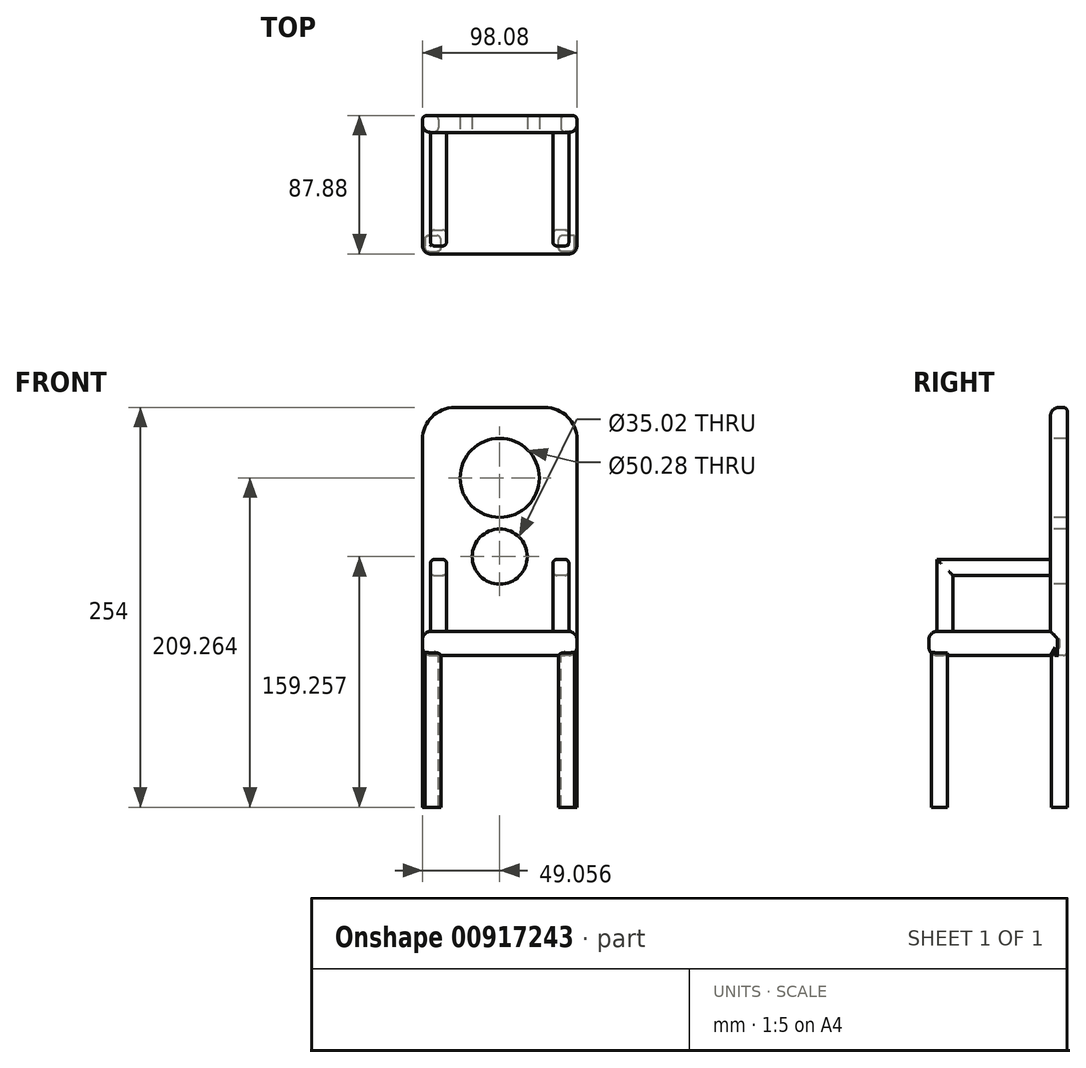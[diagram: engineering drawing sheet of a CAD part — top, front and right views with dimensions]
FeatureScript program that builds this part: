
annotation { "Feature Type Name" : "Feature", "Feature Type Description" : "" }
export const myFeature = defineFeature(function(context is Context, id is Id, definition is map)
    precondition{}
    {
        {
            var Q0;
            Q0=qCreatedBy(makeId("Top.planeOp"),FACE);
            var sketch = newSketch(context, id + "F0", { "sketchPlane" : qUnion([Q0])});
            skLineSegment(sketch, "E0.bottom", {"start": v(-206.15, 232.77) * mm, "end": v(284.07, 232.77) * mm});
            skLineSegment(sketch, "E0.top", {"start": v(-206.15, -181.25) * mm, "end": v(284.07, -181.25) * mm});
            skLineSegment(sketch, "E0.left", {"start": v(-206.15, 232.77) * mm, "end": v(-206.15, -181.25) * mm});
            skLineSegment(sketch, "E0.right", {"start": v(284.07, 232.77) * mm, "end": v(284.07, -181.25) * mm});
            skSolve(sketch);
        }
        {
            var Q0;
            Q0=qSketchRegion(id+"F0",true);
            extrude(context, id + "F1", {"entities" : qUnion([Q0]), "depth" : 76.2 * mm, "offsetDistance" : 25.4 * mm});
        }
        {
            var Q0;
            Q0=makeQuery(id+"F1.opExtrude","CAP_EDGE",EDGE,{"disambiguationData":[OSD([sQuery(id+"F0.wireOp",EDGE,"E0.top")])],"isStart":false});
            var Q1;
            Q1=makeQuery(id+"F1.opExtrude","CAP_EDGE",EDGE,{"disambiguationData":[OSD([sQuery(id+"F0.wireOp",EDGE,"E0.left")])],"isStart":false});
            var Q2;
            Q2=makeQuery(id+"F1.opExtrude","SWEPT_EDGE",EDGE,{"disambiguationData":[OSD([sQuery(id+"F0.wireOp",EDGE,"E0.top"),sQuery(id+"F0.wireOp",EDGE,"E0.left")])]});
            var Q3;
            Q3=makeQuery(id+"F1.opExtrude","SWEPT_EDGE",EDGE,{"disambiguationData":[OSD([sQuery(id+"F0.wireOp",EDGE,"E0.top"),sQuery(id+"F0.wireOp",EDGE,"E0.right")])]});
            var Q4;
            Q4=makeQuery(id+"F1.opExtrude","CAP_EDGE",EDGE,{"disambiguationData":[OSD([sQuery(id+"F0.wireOp",EDGE,"E0.right")])],"isStart":false});
            fillet(context, id + "F2", {"entities" : qUnion([Q0, Q1, Q2, Q3, Q4]), "radius" : 25.4 * mm, "tangentPropagation" : true, "allowEdgeOverflow" : false});
        }
        {
            var Q0;
            Q0=makeQuery(id+"F1.opExtrude","SWEPT_FACE",FACE,{"disambiguationData":[OSD([sQuery(id+"F0.wireOp",EDGE,"E0.bottom")])]});
            cPlane(context, id + "F3", {"entities" : qUnion([Q0]), "cplaneType" : CPlaneType.OFFSET, "offset" : 25.4 * mm, "width" : 152.4 * mm, "height" : 152.4 * mm});
        }
        {
            var Q0;
            Q0=qCreatedBy(id+"F3.planeOp",FACE);
            var sketch = newSketch(context, id + "F4", { "sketchPlane" : qUnion([Q0])});
            skLineSegment(sketch, "E1.bottom", {"start": v(-284.24, 0) * mm, "end": v(205.98, 0) * mm});
            skLineSegment(sketch, "E1.top", {"start": v(-284.24, 787.4) * mm, "end": v(205.98, 787.4) * mm});
            skLineSegment(sketch, "E1.left", {"start": v(-284.24, 0) * mm, "end": v(-284.24, 787.4) * mm});
            skLineSegment(sketch, "E1.right", {"start": v(205.98, 0) * mm, "end": v(205.98, 787.4) * mm});
            skSolve(sketch);
        }
        {
            var Q0;
            Q0=qSketchRegion(id+"F4",true);
            extrude(context, id + "F5", {"entities" : qUnion([Q0]), "operationType" : NewBodyOperationType.ADD, "oppositeDirection" : true, "depth" : 53.34 * mm, "offsetDistance" : 25.4 * mm});
        }
        {
            var Q0;
            Q0=makeQuery(id+"F5.opExtrude","SWEPT_EDGE",EDGE,{"disambiguationData":[OSD([sQuery(id+"F4.wireOp",EDGE,"E1.top"),sQuery(id+"F4.wireOp",EDGE,"E1.left")])]});
            var Q1;
            Q1=makeQuery(id+"F5.opExtrude","SWEPT_EDGE",EDGE,{"disambiguationData":[OSD([sQuery(id+"F4.wireOp",EDGE,"E1.top"),sQuery(id+"F4.wireOp",EDGE,"E1.right")])]});
            fillet(context, id + "F6", {"entities" : qUnion([Q0, Q1]), "radius" : 101.6 * mm, "tangentPropagation" : true, "allowEdgeOverflow" : false});
        }
        {
            var Q0;
            Q0=makeQuery(id+"F5.opExtrude","CAP_EDGE",EDGE,{"disambiguationData":[OSD([sQuery(id+"F4.wireOp",EDGE,"E1.left")])],"isStart":false});
            fillet(context, id + "F7", {"entities" : qUnion([Q0]), "radius" : 25.4 * mm, "tangentPropagation" : true, "allowEdgeOverflow" : false});
        }
        {
            var Q0;
            Q0=makeQuery(id+"F5.boolean.opBoolean","MERGE",FACE,{"derivedFrom":[makeQuery(id+"F1.opExtrude","CAP_FACE",FACE,{"disambiguationData":[OSD([sQuery(id+"F0.wireOp",EDGE,"E0.bottom"),sQuery(id+"F0.wireOp",EDGE,"E0.top"),sQuery(id+"F0.wireOp",EDGE,"E0.left"),sQuery(id+"F0.wireOp",EDGE,"E0.right")])],"isStart":true}),makeQuery(id+"F5.opExtrude","SWEPT_FACE",FACE,{"disambiguationData":[OSD([sQuery(id+"F4.wireOp",EDGE,"E1.bottom")])]})]});
            var sketch = newSketch(context, id + "F8", { "sketchPlane" : qUnion([Q0])});
            skLineSegment(sketch, "E2.bottom", {"start": v(-198.7, 173.81) * mm, "end": v(-147.9, 173.81) * mm});
            skLineSegment(sketch, "E2.top", {"start": v(-198.7, 123.01) * mm, "end": v(-147.9, 123.01) * mm});
            skLineSegment(sketch, "E2.left", {"start": v(-198.7, 173.81) * mm, "end": v(-198.7, 123.01) * mm});
            skLineSegment(sketch, "E2.right", {"start": v(-147.9, 173.81) * mm, "end": v(-147.9, 123.01) * mm});
            skLineSegment(sketch, "E3.bottom", {"start": v(276.63, 173.81) * mm, "end": v(225.83, 173.81) * mm});
            skLineSegment(sketch, "E3.top", {"start": v(276.63, 123.01) * mm, "end": v(225.83, 123.01) * mm});
            skLineSegment(sketch, "E3.left", {"start": v(276.63, 173.81) * mm, "end": v(276.63, 123.01) * mm});
            skLineSegment(sketch, "E3.right", {"start": v(225.83, 173.81) * mm, "end": v(225.83, 123.01) * mm});
            skLineSegment(sketch, "E4.bottom", {"start": v(284.24, -258.17) * mm, "end": v(233.44, -258.17) * mm});
            skLineSegment(sketch, "E4.top", {"start": v(284.24, -207.37) * mm, "end": v(233.44, -207.37) * mm});
            skLineSegment(sketch, "E4.left", {"start": v(284.24, -258.17) * mm, "end": v(284.24, -207.37) * mm});
            skLineSegment(sketch, "E4.right", {"start": v(233.44, -258.17) * mm, "end": v(233.44, -207.37) * mm});
            skLineSegment(sketch, "E5.bottom", {"start": v(-205.98, -258.17) * mm, "end": v(-155.18, -258.17) * mm});
            skLineSegment(sketch, "E5.top", {"start": v(-205.98, -207.37) * mm, "end": v(-155.18, -207.37) * mm});
            skLineSegment(sketch, "E5.left", {"start": v(-205.98, -258.17) * mm, "end": v(-205.98, -207.37) * mm});
            skLineSegment(sketch, "E5.right", {"start": v(-155.18, -258.17) * mm, "end": v(-155.18, -207.37) * mm});
            skSolve(sketch);
        }
        {
            var Q0;
            Q0=qSketchRegion(id+"F8",true);
            extrude(context, id + "F9", {"entities" : qUnion([Q0]), "operationType" : NewBodyOperationType.ADD, "depth" : 482.6 * mm, "offsetDistance" : 25.4 * mm});
        }
        {
            var Q0;
            Q0=makeQuery(id+"F5.opExtrude","CAP_FACE",FACE,{"disambiguationData":[OSD([sQuery(id+"F4.wireOp",EDGE,"E1.bottom"),sQuery(id+"F4.wireOp",EDGE,"E1.top"),sQuery(id+"F4.wireOp",EDGE,"E1.left"),sQuery(id+"F4.wireOp",EDGE,"E1.right")])],"isStart":false});
            var sketch = newSketch(context, id + "F10", { "sketchPlane" : qUnion([Q0])});
            skCircle(sketch, "E6", {"center": v(39.13, 563.72) * mm, "radius": 125.7 * mm});
            skPoint(sketch, "E6.centerSnap0", {"position": v(39.13, 762) * mm});
            skCircle(sketch, "E7", {"center": v(39.13, 313.69) * mm, "radius": 87.54 * mm});
            skSolve(sketch);
        }
        {
            var Q0;
            Q0=qSketchRegion(id+"F10",true);
            extrude(context, id + "F11", {"entities" : qUnion([Q0]), "operationType" : NewBodyOperationType.REMOVE, "oppositeDirection" : true, "depth" : 320.04 * mm, "offsetDistance" : 25.4 * mm});
        }
        {
            var Q0;
            Q0=makeQuery(id+"F9.opExtrude","SWEPT_EDGE",EDGE,{"disambiguationData":[OSD([sQuery(id+"F0.wireOp",EDGE,"E0.bottom"),sQuery(id+"F0.wireOp",EDGE,"E0.top"),sQuery(id+"F0.wireOp",EDGE,"E0.left"),sQuery(id+"F0.wireOp",EDGE,"E0.right"),sQuery(id+"F8.wireOp",EDGE,"E2.bottom"),sQuery(id+"F8.wireOp",EDGE,"E2.left")])]});
            var Q1;
            Q1=makeQuery(id+"F9.opExtrude","SWEPT_EDGE",EDGE,{"disambiguationData":[OSD([sQuery(id+"F8.wireOp",EDGE,"E2.bottom"),sQuery(id+"F8.wireOp",EDGE,"E2.right")])]});
            var Q2;
            Q2=makeQuery(id+"F9.opExtrude","SWEPT_EDGE",EDGE,{"disambiguationData":[OSD([sQuery(id+"F8.wireOp",EDGE,"E2.top"),sQuery(id+"F8.wireOp",EDGE,"E2.right")])]});
            var Q3;
            Q3=makeQuery(id+"F9.opExtrude","SWEPT_EDGE",EDGE,{"disambiguationData":[OSD([sQuery(id+"F8.wireOp",EDGE,"E2.top"),sQuery(id+"F8.wireOp",EDGE,"E2.left")])]});
            var Q4;
            Q4=makeQuery(id+"F9.opExtrude","SWEPT_EDGE",EDGE,{"disambiguationData":[OSD([sQuery(id+"F8.wireOp",EDGE,"E5.top"),sQuery(id+"F8.wireOp",EDGE,"E5.left")])]});
            var Q5;
            Q5=makeQuery(id+"F9.opExtrude","SWEPT_EDGE",EDGE,{"disambiguationData":[OSD([sQuery(id+"F8.wireOp",EDGE,"E5.top"),sQuery(id+"F8.wireOp",EDGE,"E5.right")])]});
            var Q6;
            Q6=makeQuery(id+"F9.boolean.opBoolean","MERGE",EDGE,{"derivedFrom":[makeQuery(id+"F5.opExtrude","CAP_EDGE",EDGE,{"disambiguationData":[OSD([sQuery(id+"F4.wireOp",EDGE,"E1.right")])],"isStart":true}),makeQuery(id+"F9.opExtrude","SWEPT_EDGE",EDGE,{"disambiguationData":[OSD([sQuery(id+"F8.wireOp",EDGE,"E5.bottom"),sQuery(id+"F8.wireOp",EDGE,"E5.left")])]})]});
            var Q7;
            Q7=makeQuery(id+"F9.opExtrude","SWEPT_EDGE",EDGE,{"disambiguationData":[OSD([sQuery(id+"F4.wireOp",EDGE,"E1.bottom"),sQuery(id+"F8.wireOp",EDGE,"E5.bottom"),sQuery(id+"F8.wireOp",EDGE,"E5.right")])]});
            var Q8;
            Q8=makeQuery(id+"F5.opExtrude","CAP_EDGE",EDGE,{"disambiguationData":[OSD([sQuery(id+"F4.wireOp",EDGE,"E1.bottom")])],"isStart":true});
            var Q9;
            Q9=makeQuery(id+"F9.opExtrude","SWEPT_EDGE",EDGE,{"disambiguationData":[OSD([sQuery(id+"F4.wireOp",EDGE,"E1.bottom"),sQuery(id+"F8.wireOp",EDGE,"E4.bottom"),sQuery(id+"F8.wireOp",EDGE,"E4.right")])]});
            var Q10;
            Q10=makeQuery(id+"F9.boolean.opBoolean","MERGE",EDGE,{"derivedFrom":[makeQuery(id+"F5.opExtrude","CAP_EDGE",EDGE,{"disambiguationData":[OSD([sQuery(id+"F4.wireOp",EDGE,"E1.left")])],"isStart":true}),makeQuery(id+"F9.opExtrude","SWEPT_EDGE",EDGE,{"disambiguationData":[OSD([sQuery(id+"F8.wireOp",EDGE,"E4.bottom"),sQuery(id+"F8.wireOp",EDGE,"E4.left")])]})]});
            var Q11;
            Q11=makeQuery(id+"F9.opExtrude","SWEPT_EDGE",EDGE,{"disambiguationData":[OSD([sQuery(id+"F8.wireOp",EDGE,"E4.top"),sQuery(id+"F8.wireOp",EDGE,"E4.left")])]});
            var Q12;
            Q12=makeQuery(id+"F9.opExtrude","SWEPT_EDGE",EDGE,{"disambiguationData":[OSD([sQuery(id+"F8.wireOp",EDGE,"E4.top"),sQuery(id+"F8.wireOp",EDGE,"E4.right")])]});
            var Q13;
            Q13=makeQuery(id+"F9.opExtrude","SWEPT_EDGE",EDGE,{"disambiguationData":[OSD([sQuery(id+"F8.wireOp",EDGE,"E3.bottom"),sQuery(id+"F8.wireOp",EDGE,"E3.right")])]});
            var Q14;
            Q14=makeQuery(id+"F9.opExtrude","SWEPT_EDGE",EDGE,{"disambiguationData":[OSD([sQuery(id+"F8.wireOp",EDGE,"E3.top"),sQuery(id+"F8.wireOp",EDGE,"E3.right")])]});
            var Q15;
            Q15=makeQuery(id+"F9.opExtrude","SWEPT_EDGE",EDGE,{"disambiguationData":[OSD([sQuery(id+"F0.wireOp",EDGE,"E0.bottom"),sQuery(id+"F0.wireOp",EDGE,"E0.top"),sQuery(id+"F0.wireOp",EDGE,"E0.left"),sQuery(id+"F0.wireOp",EDGE,"E0.right"),sQuery(id+"F8.wireOp",EDGE,"E3.bottom"),sQuery(id+"F8.wireOp",EDGE,"E3.left")])]});
            fillet(context, id + "F12", {"entities" : qUnion([Q0, Q1, Q2, Q3, Q4, Q5, Q6, Q7, Q8, Q9, Q10, Q11, Q12, Q13, Q14, Q15]), "radius" : 12.7 * mm, "tangentPropagation" : true, "allowEdgeOverflow" : false});
        }
        {
            var Q0;
            Q0=makeQuery(id+"F1.opExtrude","CAP_EDGE",EDGE,{"disambiguationData":[OSD([sQuery(id+"F0.wireOp",EDGE,"E0.top")])],"isStart":true});
            fillet(context, id + "F13", {"entities" : qUnion([Q0]), "radius" : 25.4 * mm, "tangentPropagation" : true, "allowEdgeOverflow" : false});
        }
        {
            var Q0;
            Q0=makeQuery(id+"F11.boolean.opBoolean","COPY",EDGE,{"derivedFrom":makeQuery(id+"F11.opExtrude","CAP_EDGE",EDGE,{"disambiguationData":[OSD([sQuery(id+"F10.wireOp",EDGE,"E6")])],"isStart":true})});
            var Q1;
            Q1=makeQuery(id+"F11.boolean.opBoolean","INTERSECT",EDGE,{"derivedFrom":[makeQuery(id+"F9.boolean.opBoolean","MERGE",FACE,{"derivedFrom":[makeQuery(id+"F5.opExtrude","CAP_FACE",FACE,{"disambiguationData":[OSD([sQuery(id+"F4.wireOp",EDGE,"E1.bottom"),sQuery(id+"F4.wireOp",EDGE,"E1.top"),sQuery(id+"F4.wireOp",EDGE,"E1.left"),sQuery(id+"F4.wireOp",EDGE,"E1.right")])],"isStart":true}),makeQuery(id+"F9.opExtrude","SWEPT_FACE",FACE,{"disambiguationData":[OSD([sQuery(id+"F8.wireOp",EDGE,"E4.bottom")])]}),makeQuery(id+"F9.opExtrude","SWEPT_FACE",FACE,{"disambiguationData":[OSD([sQuery(id+"F8.wireOp",EDGE,"E5.bottom")])]})]}),makeQuery(id+"F11.opExtrude","SWEPT_FACE",FACE,{"disambiguationData":[OSD([sQuery(id+"F10.wireOp",EDGE,"E6")])]})]});
            fillet(context, id + "F14", {"entities" : qUnion([Q0, Q1]), "radius" : 5.08 * mm, "tangentPropagation" : true, "allowEdgeOverflow" : false});
        }
        {
            var Q0;
            Q0=makeQuery(id+"F1.opExtrude","CAP_FACE",FACE,{"disambiguationData":[OSD([sQuery(id+"F0.wireOp",EDGE,"E0.bottom"),sQuery(id+"F0.wireOp",EDGE,"E0.top"),sQuery(id+"F0.wireOp",EDGE,"E0.left"),sQuery(id+"F0.wireOp",EDGE,"E0.right")])],"isStart":false});
            var sketch = newSketch(context, id + "F15", { "sketchPlane" : qUnion([Q0])});
            skLineSegment(sketch, "E8.bottom", {"start": v(258.67, -155.85) * mm, "end": v(207.87, -155.85) * mm});
            skLineSegment(sketch, "E8.top", {"start": v(258.67, -105.05) * mm, "end": v(207.87, -105.05) * mm});
            skLineSegment(sketch, "E8.left", {"start": v(258.67, -155.85) * mm, "end": v(258.67, -105.05) * mm});
            skLineSegment(sketch, "E8.right", {"start": v(207.87, -155.85) * mm, "end": v(207.87, -105.05) * mm});
            skLineSegment(sketch, "E9.bottom", {"start": v(-180.75, -155.85) * mm, "end": v(-129.95, -155.85) * mm});
            skLineSegment(sketch, "E9.top", {"start": v(-180.75, -105.05) * mm, "end": v(-129.95, -105.05) * mm});
            skLineSegment(sketch, "E9.left", {"start": v(-180.75, -155.85) * mm, "end": v(-180.75, -105.05) * mm});
            skLineSegment(sketch, "E9.right", {"start": v(-129.95, -155.85) * mm, "end": v(-129.95, -105.05) * mm});
            skSolve(sketch);
        }
        {
            var Q0;
            Q0=qSketchRegion(id+"F15",true);
            extrude(context, id + "F16", {"entities" : qUnion([Q0]), "operationType" : NewBodyOperationType.ADD, "depth" : 228.6 * mm, "offsetDistance" : 25.4 * mm});
        }
        {
            var Q0;
            Q0=makeQuery(id+"F16.opExtrude","SWEPT_FACE",FACE,{"disambiguationData":[OSD([sQuery(id+"F15.wireOp",EDGE,"E9.top")])]});
            var sketch = newSketch(context, id + "F17", { "sketchPlane" : qUnion([Q0])});
            skLineSegment(sketch, "E10.bottom", {"start": v(129.95, 304.8) * mm, "end": v(180.75, 304.8) * mm});
            skLineSegment(sketch, "E10.top", {"start": v(129.95, 254) * mm, "end": v(180.75, 254) * mm});
            skLineSegment(sketch, "E10.left", {"start": v(129.95, 304.8) * mm, "end": v(129.95, 254) * mm});
            skLineSegment(sketch, "E10.right", {"start": v(180.75, 304.8) * mm, "end": v(180.75, 254) * mm});
            skSolve(sketch);
        }
        {
            var Q0;
            Q0=qSketchRegion(id+"F17",true);
            extrude(context, id + "F18", {"entities" : qUnion([Q0]), "operationType" : NewBodyOperationType.ADD, "depth" : 355.6 * mm, "offsetDistance" : 25.4 * mm});
        }
        {
            var Q0;
            Q0=makeQuery(id+"F16.opExtrude","SWEPT_FACE",FACE,{"disambiguationData":[OSD([sQuery(id+"F15.wireOp",EDGE,"E8.top")])]});
            var sketch = newSketch(context, id + "F19", { "sketchPlane" : qUnion([Q0])});
            skLineSegment(sketch, "E11.bottom", {"start": v(-258.67, 304.8) * mm, "end": v(-207.87, 304.8) * mm});
            skLineSegment(sketch, "E11.top", {"start": v(-258.67, 254) * mm, "end": v(-207.87, 254) * mm});
            skLineSegment(sketch, "E11.left", {"start": v(-258.67, 304.8) * mm, "end": v(-258.67, 254) * mm});
            skLineSegment(sketch, "E11.right", {"start": v(-207.87, 304.8) * mm, "end": v(-207.87, 254) * mm});
            skSolve(sketch);
        }
        {
            var Q0;
            Q0=qSketchRegion(id+"F19",true);
            extrude(context, id + "F20", {"entities" : qUnion([Q0]), "operationType" : NewBodyOperationType.ADD, "depth" : 355.6 * mm, "offsetDistance" : 25.4 * mm});
        }
        {
            var Q0;
            Q0=makeQuery(id+"F16.opExtrude","SWEPT_EDGE",EDGE,{"disambiguationData":[OSD([sQuery(id+"F0.wireOp",EDGE,"E0.bottom"),sQuery(id+"F0.wireOp",EDGE,"E0.top"),sQuery(id+"F0.wireOp",EDGE,"E0.left"),sQuery(id+"F0.wireOp",EDGE,"E0.right"),sQuery(id+"F15.wireOp",EDGE,"E9.bottom"),sQuery(id+"F15.wireOp",EDGE,"E9.right")])]});
            var Q1;
            Q1=makeQuery(id+"F16.opExtrude","SWEPT_EDGE",EDGE,{"disambiguationData":[OSD([sQuery(id+"F15.wireOp",EDGE,"E9.bottom"),sQuery(id+"F15.wireOp",EDGE,"E9.left")])]});
            var Q2;
            Q2=makeQuery(id+"F16.opExtrude","SWEPT_EDGE",EDGE,{"disambiguationData":[OSD([sQuery(id+"F0.wireOp",EDGE,"E0.bottom"),sQuery(id+"F0.wireOp",EDGE,"E0.top"),sQuery(id+"F0.wireOp",EDGE,"E0.left"),sQuery(id+"F0.wireOp",EDGE,"E0.right"),sQuery(id+"F15.wireOp",EDGE,"E9.top"),sQuery(id+"F15.wireOp",EDGE,"E9.left")])]});
            var Q3;
            Q3=makeQuery(id+"F18.opExtrude","SWEPT_EDGE",EDGE,{"disambiguationData":[OSD([sQuery(id+"F0.wireOp",EDGE,"E0.bottom"),sQuery(id+"F0.wireOp",EDGE,"E0.top"),sQuery(id+"F0.wireOp",EDGE,"E0.left"),sQuery(id+"F0.wireOp",EDGE,"E0.right"),sQuery(id+"F15.wireOp",EDGE,"E9.top"),sQuery(id+"F15.wireOp",EDGE,"E9.left"),sQuery(id+"F17.wireOp",EDGE,"E10.top"),sQuery(id+"F17.wireOp",EDGE,"E10.right")])]});
            var Q4;
            Q4=makeQuery(id+"F18.boolean.opBoolean","MERGE",EDGE,{"derivedFrom":[makeQuery(id+"F16.opExtrude","CAP_EDGE",EDGE,{"disambiguationData":[OSD([sQuery(id+"F15.wireOp",EDGE,"E9.left")])],"isStart":false}),makeQuery(id+"F18.opExtrude","SWEPT_EDGE",EDGE,{"disambiguationData":[OSD([sQuery(id+"F17.wireOp",EDGE,"E10.bottom"),sQuery(id+"F17.wireOp",EDGE,"E10.right")])]})]});
            var Q5;
            Q5=makeQuery(id+"F18.boolean.opBoolean","MERGE",EDGE,{"derivedFrom":[makeQuery(id+"F16.opExtrude","CAP_EDGE",EDGE,{"disambiguationData":[OSD([sQuery(id+"F15.wireOp",EDGE,"E9.right")])],"isStart":false}),makeQuery(id+"F18.opExtrude","SWEPT_EDGE",EDGE,{"disambiguationData":[OSD([sQuery(id+"F17.wireOp",EDGE,"E10.bottom"),sQuery(id+"F17.wireOp",EDGE,"E10.left")])]})]});
            var Q6;
            Q6=makeQuery(id+"F18.opExtrude","SWEPT_EDGE",EDGE,{"disambiguationData":[OSD([sQuery(id+"F15.wireOp",EDGE,"E9.top"),sQuery(id+"F15.wireOp",EDGE,"E9.right"),sQuery(id+"F17.wireOp",EDGE,"E10.top"),sQuery(id+"F17.wireOp",EDGE,"E10.left")])]});
            var Q7;
            Q7=makeQuery(id+"F16.opExtrude","SWEPT_EDGE",EDGE,{"disambiguationData":[OSD([sQuery(id+"F15.wireOp",EDGE,"E9.top"),sQuery(id+"F15.wireOp",EDGE,"E9.right")])]});
            var Q8;
            Q8=makeQuery(id+"F20.boolean.opBoolean","MERGE",EDGE,{"derivedFrom":[makeQuery(id+"F16.opExtrude","CAP_EDGE",EDGE,{"disambiguationData":[OSD([sQuery(id+"F15.wireOp",EDGE,"E8.left")])],"isStart":false}),makeQuery(id+"F20.opExtrude","SWEPT_EDGE",EDGE,{"disambiguationData":[OSD([sQuery(id+"F19.wireOp",EDGE,"E11.bottom"),sQuery(id+"F19.wireOp",EDGE,"E11.left")])]})]});
            var Q9;
            Q9=makeQuery(id+"F20.boolean.opBoolean","MERGE",EDGE,{"derivedFrom":[makeQuery(id+"F16.opExtrude","CAP_EDGE",EDGE,{"disambiguationData":[OSD([sQuery(id+"F15.wireOp",EDGE,"E8.right")])],"isStart":false}),makeQuery(id+"F20.opExtrude","SWEPT_EDGE",EDGE,{"disambiguationData":[OSD([sQuery(id+"F19.wireOp",EDGE,"E11.bottom"),sQuery(id+"F19.wireOp",EDGE,"E11.right")])]})]});
            var Q10;
            Q10=makeQuery(id+"F16.opExtrude","SWEPT_EDGE",EDGE,{"disambiguationData":[OSD([sQuery(id+"F0.wireOp",EDGE,"E0.bottom"),sQuery(id+"F0.wireOp",EDGE,"E0.top"),sQuery(id+"F0.wireOp",EDGE,"E0.left"),sQuery(id+"F0.wireOp",EDGE,"E0.right"),sQuery(id+"F15.wireOp",EDGE,"E8.bottom"),sQuery(id+"F15.wireOp",EDGE,"E8.right")])]});
            var Q11;
            Q11=makeQuery(id+"F16.opExtrude","SWEPT_EDGE",EDGE,{"disambiguationData":[OSD([sQuery(id+"F15.wireOp",EDGE,"E8.bottom"),sQuery(id+"F15.wireOp",EDGE,"E8.left")])]});
            var Q12;
            Q12=makeQuery(id+"F16.opExtrude","SWEPT_EDGE",EDGE,{"disambiguationData":[OSD([sQuery(id+"F0.wireOp",EDGE,"E0.bottom"),sQuery(id+"F0.wireOp",EDGE,"E0.top"),sQuery(id+"F0.wireOp",EDGE,"E0.left"),sQuery(id+"F0.wireOp",EDGE,"E0.right"),sQuery(id+"F15.wireOp",EDGE,"E8.top"),sQuery(id+"F15.wireOp",EDGE,"E8.left")])]});
            var Q13;
            Q13=makeQuery(id+"F20.opExtrude","SWEPT_EDGE",EDGE,{"disambiguationData":[OSD([sQuery(id+"F0.wireOp",EDGE,"E0.bottom"),sQuery(id+"F0.wireOp",EDGE,"E0.top"),sQuery(id+"F0.wireOp",EDGE,"E0.left"),sQuery(id+"F0.wireOp",EDGE,"E0.right"),sQuery(id+"F15.wireOp",EDGE,"E8.top"),sQuery(id+"F15.wireOp",EDGE,"E8.left"),sQuery(id+"F19.wireOp",EDGE,"E11.top"),sQuery(id+"F19.wireOp",EDGE,"E11.left")])]});
            var Q14;
            Q14=makeQuery(id+"F20.opExtrude","SWEPT_EDGE",EDGE,{"disambiguationData":[OSD([sQuery(id+"F15.wireOp",EDGE,"E8.top"),sQuery(id+"F15.wireOp",EDGE,"E8.right"),sQuery(id+"F19.wireOp",EDGE,"E11.top"),sQuery(id+"F19.wireOp",EDGE,"E11.right")])]});
            var Q15;
            Q15=makeQuery(id+"F16.opExtrude","SWEPT_EDGE",EDGE,{"disambiguationData":[OSD([sQuery(id+"F15.wireOp",EDGE,"E8.top"),sQuery(id+"F15.wireOp",EDGE,"E8.right")])]});
            fillet(context, id + "F21", {"entities" : qUnion([Q0, Q1, Q2, Q3, Q4, Q5, Q6, Q7, Q8, Q9, Q10, Q11, Q12, Q13, Q14, Q15]), "radius" : 12.7 * mm, "tangentPropagation" : true, "allowEdgeOverflow" : false});
        }
        {
            var Q0;
            Q0=makeQuery(id+"F11.boolean.opBoolean","INTERSECT",EDGE,{"derivedFrom":[makeQuery(id+"F9.boolean.opBoolean","MERGE",FACE,{"derivedFrom":[makeQuery(id+"F5.opExtrude","CAP_FACE",FACE,{"disambiguationData":[OSD([sQuery(id+"F4.wireOp",EDGE,"E1.bottom"),sQuery(id+"F4.wireOp",EDGE,"E1.top"),sQuery(id+"F4.wireOp",EDGE,"E1.left"),sQuery(id+"F4.wireOp",EDGE,"E1.right")])],"isStart":true}),makeQuery(id+"F9.opExtrude","SWEPT_FACE",FACE,{"disambiguationData":[OSD([sQuery(id+"F8.wireOp",EDGE,"E4.bottom")])]}),makeQuery(id+"F9.opExtrude","SWEPT_FACE",FACE,{"disambiguationData":[OSD([sQuery(id+"F8.wireOp",EDGE,"E5.bottom")])]})]}),makeQuery(id+"F11.opExtrude","SWEPT_FACE",FACE,{"disambiguationData":[OSD([sQuery(id+"F10.wireOp",EDGE,"E7")])]})]});
            var Q1;
            Q1=makeQuery(id+"F11.boolean.opBoolean","COPY",EDGE,{"derivedFrom":makeQuery(id+"F11.opExtrude","CAP_EDGE",EDGE,{"disambiguationData":[OSD([sQuery(id+"F10.wireOp",EDGE,"E7")])],"isStart":true})});
            fillet(context, id + "F22", {"entities" : qUnion([Q0, Q1]), "radius" : 5.08 * mm, "tangentPropagation" : true, "allowEdgeOverflow" : false});
        }
        {
            var Q0;
            {var subQ0=sQuery(id+"F0.wireOp",EDGE,"E0.top");Q0=makeQuery(id+"F13.opFillet","BLEND_EDGE",EDGE,{"blendedFrom":[makeQuery(id+"F1.opExtrude","CAP_EDGE",EDGE,{"disambiguationData":[OSD([subQ0])],"isStart":true}),makeQuery(id+"F1.opExtrude","SWEPT_FACE",FACE,{"disambiguationData":[OSD([subQ0])]})],"blendedInto":[makeQuery(id+"F1.opExtrude","SWEPT_FACE",FACE,{"disambiguationData":[OSD([subQ0])]})]});}
            cPoint(context, id + "F23", {"entities" : qUnion([Q0]), "parameter" : 0.5});
        }
        {
            var Q0;
            Q0=makeQuery(id+"F1.opExtrude","SWEPT_BODY",BODY,{"disambiguationData":[OSD([sQuery(id+"F0.wireOp",EDGE,"E0.bottom"),sQuery(id+"F0.wireOp",EDGE,"E0.top"),sQuery(id+"F0.wireOp",EDGE,"E0.left"),sQuery(id+"F0.wireOp",EDGE,"E0.right")])]});
            var Q1;
            Q1 = qCreatedBy(id + "F23" ,VERTEX);
            var Q2;
            Q2=qCreatedBy(makeId("Origin.pointOp"),VERTEX);
            transform(context, id + "F24", {"entities" : qUnion([Q0]), "transformType" : TransformType.SCALE_UNIFORMLY, "scale" : .2, "scalePoint" : qUnion([Q2]), "makeCopy" : false});
        }
    });
